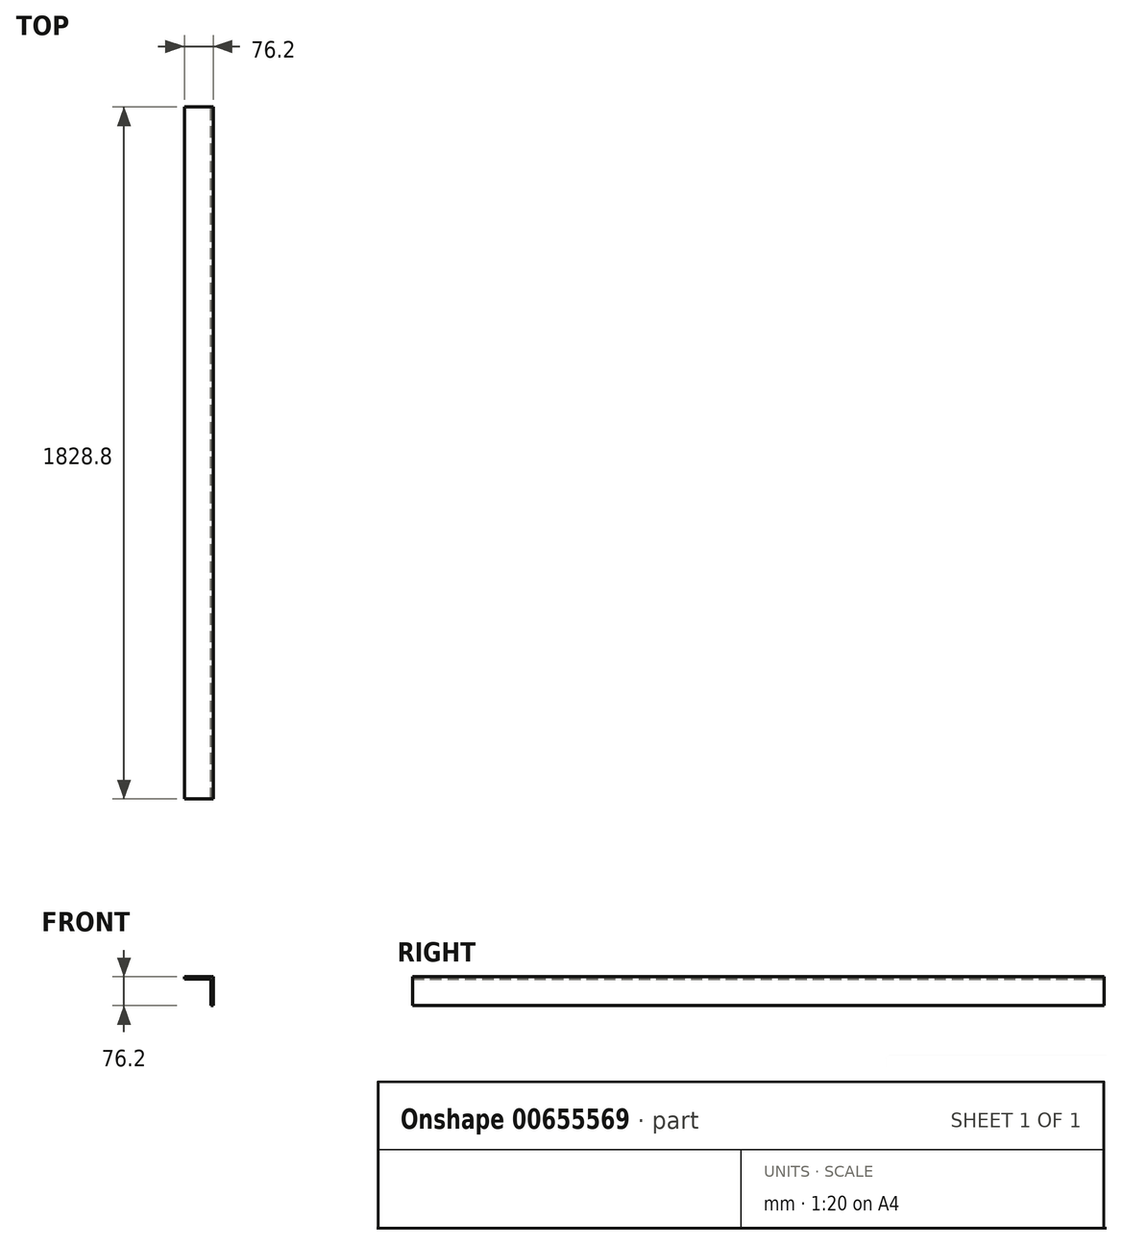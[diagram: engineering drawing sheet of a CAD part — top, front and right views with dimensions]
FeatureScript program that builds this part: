
annotation { "Feature Type Name" : "Feature", "Feature Type Description" : "" }
export const myFeature = defineFeature(function(context is Context, id is Id, definition is map)
    precondition{}
    {
        {
            var Q0;
            Q0=qCreatedBy(makeId("Front.planeOp"),FACE);
            var sketch = newSketch(context, id + "F0", { "sketchPlane" : qUnion([Q0])});
            skLineSegment(sketch, "E0", {"start": v(37.28, 33) * mm, "end": v(113.48, 33) * mm});
            skLineSegment(sketch, "E1", {"start": v(113.48, 33) * mm, "end": v(113.48, -43.2) * mm});
            skLineSegment(sketch, "E2", {"start": v(37.28, 33) * mm, "end": v(37.28, 26.65) * mm});
            skLineSegment(sketch, "E3", {"start": v(37.28, 26.65) * mm, "end": v(107.13, 26.65) * mm});
            skLineSegment(sketch, "E4", {"start": v(107.13, 26.65) * mm, "end": v(107.13, -43.2) * mm});
            skLineSegment(sketch, "E5", {"start": v(107.13, -43.2) * mm, "end": v(113.48, -43.2) * mm});
            skSolve(sketch);
        }
        {
            var Q0;
            Q0 = qSketchRegion(id + "F0", true);
            extrude(context, id + "F1", {"entities" : qUnion([Q0]), "depth" : 1828.8 * mm, "offsetDistance" : 25.4 * mm});
        }
    });
